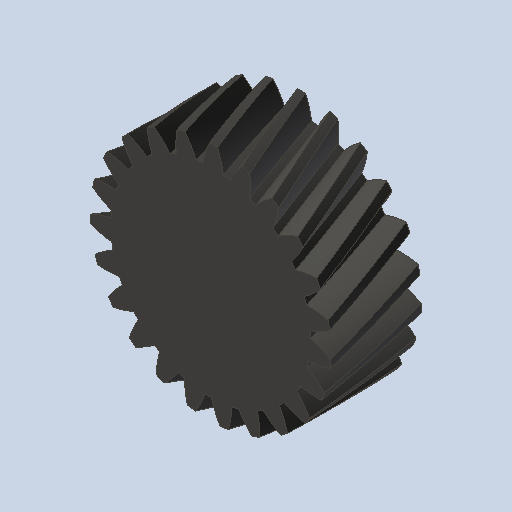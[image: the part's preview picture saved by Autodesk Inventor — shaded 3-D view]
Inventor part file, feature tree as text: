
AUTODESK INVENTOR PART (.ipt)
format: ipt  version: 2023 (Build 270158000, 158)  size: 456,192 bytes
history: native  units: mm (DEFAULTED — no unit token found)
features: plane x3, other x3, sketch x2, extrude x1
ambient origin geometry x8: Origin, YZ Plane, XZ Plane, XY Plane, X Axis, Y Axis, Z Axis, Center Point
bodies: Solid1 (feature_tree)
feature tree (9):
  extrude  "Extrusion1"  Depth=10.0mm TaperAngle=0.0deg
  plane  "Work Plane2"
  plane  "Work Plane8"
  plane  "Work Plane9"
  other  "Spur Gear"
  sketch  "Sketch1"  dims[d0=26.475835mm d1=10.0mm d2=0.0mm]
  sketch  "Sketch2"  dims[d3=24.476089mm d4=10.0mm d5=0.0mm d16=107.95mm d17=0.0mm d34=1.36591mm d39=0.0mm d41=0.0mm d43=107.95mm d46=107.95mm d47=0.0mm d48=0.0mm]
  other  "Srf1"
  other  "Pitch Diameter"
